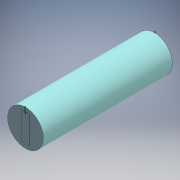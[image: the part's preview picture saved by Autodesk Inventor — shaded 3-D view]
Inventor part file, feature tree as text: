
AUTODESK INVENTOR PART (.ipt)
format: ipt  version: 2016 (Build 200138000, 138)  size: 171,520 bytes
history: native  units: mm
features: extrude x3, sketch x3, fillet x2, other x1, mirror x1
ambient origin geometry x8: Origin, YZ Plane, XZ Plane, XY Plane, X Axis, Y Axis, Z Axis, Center Point
bodies: Body1 (feature_tree)
feature tree (10):
  other  "Sólido1"
  extrude  "Extrusión1"  Depth=0.1mm TaperAngle=0.0deg
  extrude  "Extrusión2"  Depth=0.2mm
  extrude  "Extrusión3"  [1 undecoded]
  fillet  "Empalme1"  [1 undecoded]
  fillet  "Empalme2"  [1 undecoded]
  mirror  "Simetría1"
  sketch  "Boceto1"  dims[d1=32.5mm d2=0.0mm d7=0.1mm d8=0.0mm]
  sketch  "Boceto3"  dims[d13=0.2mm d14=0.0mm d15=0.2mm]
  sketch  "Boceto4"  dims[d16=0.02mm]
note: 3 required parameter values undecoded (feature->parameter linkage not recoverable at this tier; creation-order binding heuristic only, values carry confidence <= 0.55)
